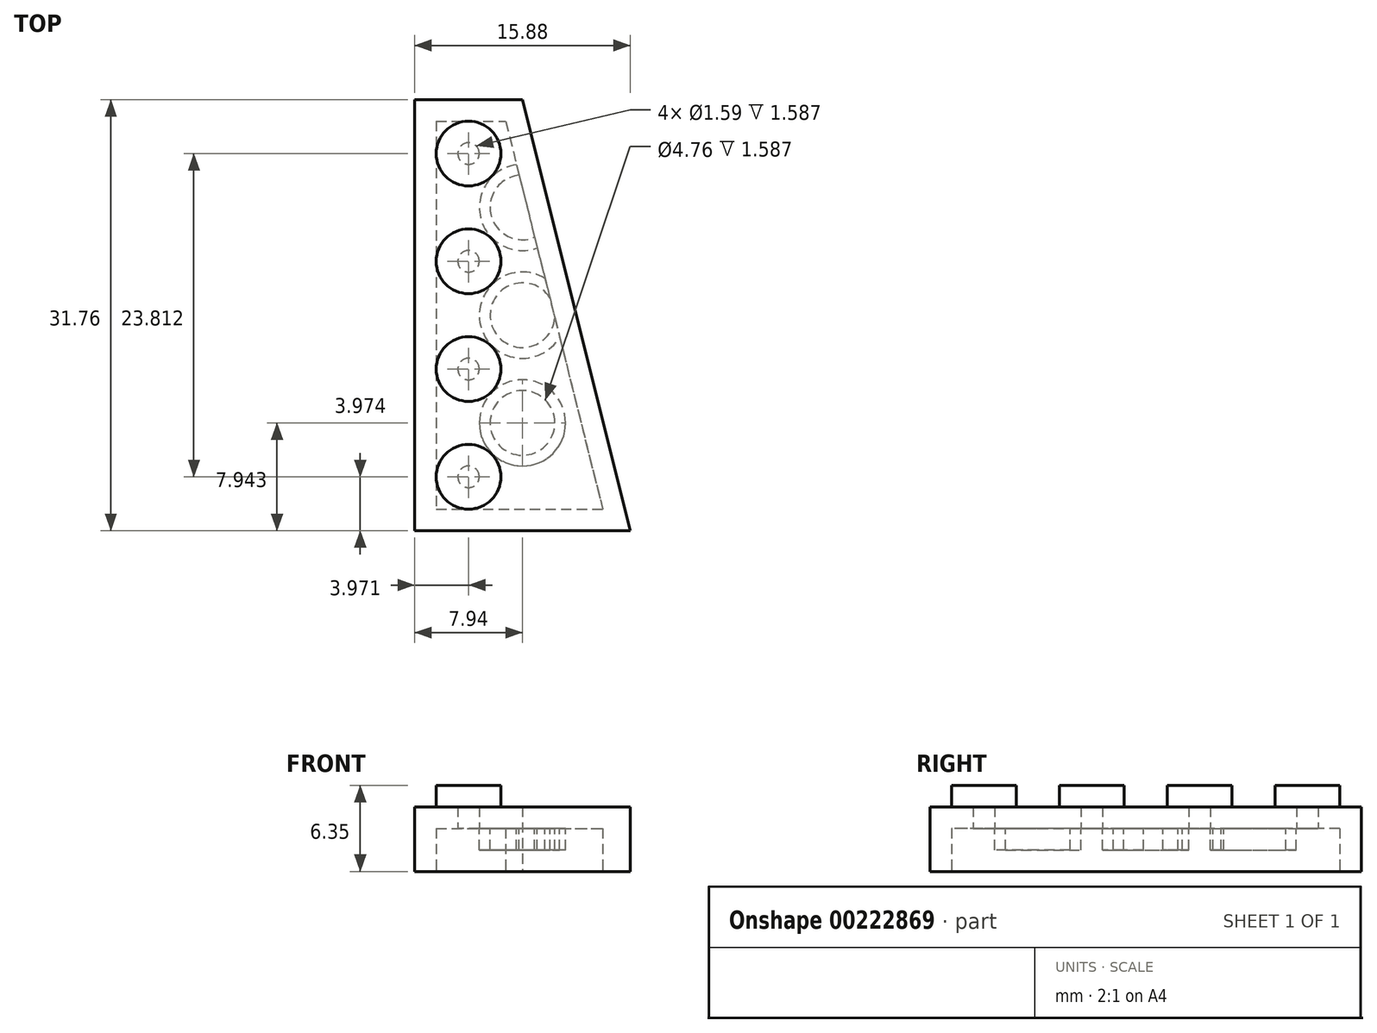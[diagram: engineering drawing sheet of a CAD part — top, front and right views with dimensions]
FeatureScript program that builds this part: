
annotation { "Feature Type Name" : "Feature", "Feature Type Description" : "" }
export const myFeature = defineFeature(function(context is Context, id is Id, definition is map)
    precondition{}
    {
        {
            var Q0;
            Q0=qCreatedBy(makeId("Top.planeOp"),FACE);
            var sketch = newSketch(context, id + "F0", { "sketchPlane" : qUnion([Q0])});
            skLineSegment(sketch, "E0.bottom", {"start": v(-7.94, 15.88) * mm, "end": v(7.94, 15.88) * mm});
            skLineSegment(sketch, "E0.top", {"start": v(-7.94, -15.88) * mm, "end": v(7.94, -15.88) * mm});
            skLineSegment(sketch, "E0.left", {"start": v(-7.94, 15.88) * mm, "end": v(-7.94, -15.88) * mm});
            skLineSegment(sketch, "E0.right", {"start": v(7.94, 15.88) * mm, "end": v(7.94, -15.88) * mm});
            skPoint(sketch, "E0.middle", {"position": v(0, 0) * mm});
            skCircle(sketch, "E1", {"center": v(-3.97, -11.9) * mm, "radius": 2.38 * mm});
            skCircle(sketch, "E2.0.1.0", {"center": v(-3.97, -3.97) * mm, "radius": 2.38 * mm});
            skLineSegment(sketch, "E2.direction1", {"start": v(-3.97, -11.9) * mm, "end": v(29.37, -11.9) * mm, "construction": true});
            skLineSegment(sketch, "E2.direction2", {"start": v(-3.97, -11.9) * mm, "end": v(-3.97, -3.97) * mm, "construction": true});
            skCircle(sketch, "E3.0.0.2", {"center": v(-3.97, 3.97) * mm, "radius": 2.38 * mm});
            skCircle(sketch, "E3.0.0.3", {"center": v(-3.97, 11.9) * mm, "radius": 2.38 * mm});
            skPoint(sketch, "E4", {"position": v(0, 15.88) * mm});
            skLineSegment(sketch, "E5", {"start": v(0, 15.87) * mm, "end": v(7.94, -15.87) * mm});
            skSolve(sketch);
        }
        {
            var Q0;
            Q0=makeQuery(id+"F0.imprint","IMPRINT",FACE,{"disambiguationData":[TD([[makeQuery(id+"F0.imprint","IMPRINT",EDGE,{"derivedFrom":sQuery(id+"F0.wireOp",EDGE,"E0.top")}),1.0]])]});
            extrude(context, id + "F1", {"entities" : qUnion([Q0]), "depth" : 3.17 * mm});
        }
        {
            var Q0;
            Q0=makeQuery(id+"F0.imprint","IMPRINT",FACE,{"disambiguationData":[TD([[makeQuery(id+"F0.imprint","IMPRINT",EDGE,{"derivedFrom":sQuery(id+"F0.wireOp",EDGE,"E3.0.0.3")}),1.0]])]});
            var Q1;
            Q1=makeQuery(id+"F0.imprint","IMPRINT",FACE,{"disambiguationData":[TD([[makeQuery(id+"F0.imprint","IMPRINT",EDGE,{"derivedFrom":sQuery(id+"F0.wireOp",EDGE,"E3.0.0.2")}),1.0]])]});
            var Q2;
            Q2=makeQuery(id+"F0.imprint","IMPRINT",FACE,{"disambiguationData":[TD([[makeQuery(id+"F0.imprint","IMPRINT",EDGE,{"derivedFrom":sQuery(id+"F0.wireOp",EDGE,"E2.0.1.0")}),1.0]])]});
            var Q3;
            Q3=makeQuery(id+"F0.imprint","IMPRINT",FACE,{"disambiguationData":[TD([[makeQuery(id+"F0.imprint","IMPRINT",EDGE,{"derivedFrom":sQuery(id+"F0.wireOp",EDGE,"E1")}),1.0]])]});
            extrude(context, id + "F2", {"entities" : qUnion([Q0, Q1, Q2, Q3]), "operationType" : NewBodyOperationType.ADD, "depth" : 4.76 * mm});
        }
        {
            var Q0;
            {var subQ0=sQuery(id+"F0.wireOp",EDGE,"E3.0.0.3");var subQ1=sQuery(id+"F0.wireOp",EDGE,"E3.0.0.2");var subQ2=sQuery(id+"F0.wireOp",EDGE,"E2.0.1.0");var subQ3=sQuery(id+"F0.wireOp",EDGE,"E1");Q0=makeQuery(id+"F2.boolean.opBoolean","MERGE",FACE,{"derivedFrom":[makeQuery(id+"F1.opExtrude","CAP_FACE",FACE,{"disambiguationData":[OSD([sQuery(id+"F0.wireOp",EDGE,"E0.bottom"),sQuery(id+"F0.wireOp",EDGE,"E0.top"),sQuery(id+"F0.wireOp",EDGE,"E0.left"),sQuery(id+"F0.wireOp",EDGE,"E0.right"),subQ3,subQ2,subQ1,subQ0])],"isStart":true}),makeQuery(id+"F2.opExtrude","CAP_FACE",FACE,{"disambiguationData":[OSD([subQ3])],"isStart":true}),makeQuery(id+"F2.opExtrude","CAP_FACE",FACE,{"disambiguationData":[OSD([subQ2])],"isStart":true}),makeQuery(id+"F2.opExtrude","CAP_FACE",FACE,{"disambiguationData":[OSD([subQ1])],"isStart":true}),makeQuery(id+"F2.opExtrude","CAP_FACE",FACE,{"disambiguationData":[OSD([subQ0])],"isStart":true})]});}
            shell(context, id + "F3", {"entities" : qUnion([Q0]), "thickness" : 1.59 * mm});
        }
        {
            var Q0;
            Q0=makeQuery(id+"F3.opShell","OFFSET_FACE",FACE,{"disambiguationData":[OSD([sQuery(id+"F0.wireOp",EDGE,"E0.bottom"),sQuery(id+"F0.wireOp",EDGE,"E0.top"),sQuery(id+"F0.wireOp",EDGE,"E0.left"),sQuery(id+"F0.wireOp",EDGE,"E1"),sQuery(id+"F0.wireOp",EDGE,"E2.0.1.0"),sQuery(id+"F0.wireOp",EDGE,"E3.0.0.2"),sQuery(id+"F0.wireOp",EDGE,"E3.0.0.3"),sQuery(id+"F0.wireOp",EDGE,"E5")])]});
            var sketch = newSketch(context, id + "F4", { "sketchPlane" : qUnion([Q0])});
            skCircle(sketch, "E6", {"center": v(0, -7.94) * mm, "radius": 3.18 * mm});
            skCircle(sketch, "E7", {"center": v(0, -7.94) * mm, "radius": 2.38 * mm});
            skCircle(sketch, "E8.0.1.0", {"center": v(0, 0) * mm, "radius": 3.18 * mm});
            skCircle(sketch, "E8.0.1.1", {"center": v(0, 0) * mm, "radius": 2.38 * mm});
            skCircle(sketch, "E8.0.2.0", {"center": v(0, 7.94) * mm, "radius": 3.18 * mm});
            skCircle(sketch, "E8.0.2.1", {"center": v(0, 7.94) * mm, "radius": 2.38 * mm});
            skLineSegment(sketch, "E8.direction1", {"start": v(0, -7.94) * mm, "end": v(25.4, -7.94) * mm, "construction": true});
            skLineSegment(sketch, "E8.direction2", {"start": v(0, -7.94) * mm, "end": v(0, 0) * mm, "construction": true});
            skSolve(sketch);
        }
        {
            var Q0;
            Q0=makeQuery(id+"F4.imprint","IMPRINT",FACE,{"disambiguationData":[TD([[makeQuery(id+"F4.imprint","IMPRINT",EDGE,{"derivedFrom":sQuery(id+"F4.wireOp",EDGE,"E8.0.2.0")}),1.0]])]});
            var Q1;
            {var subQ0=sQuery(id+"F4.wireOp",EDGE,"E8.0.1.0");var subQ1=sQuery(id+"F0.wireOp",EDGE,"Vv1mUmgO-7Zh7-OptV-hwL2-uFvwZgxB2kij");var subQ2=makeQuery(id+"F3.opShell","OFFSET_EDGE",EDGE,{"disambiguationData":[OSD([subQ1]),TDD([makeQuery(id+"F1.opExtrude","CAP_EDGE",EDGE,{"disambiguationData":[OSD([subQ1])],"isStart":false})])]});var subQ3=makeQuery(id+"F4.imprint","INTERSECT",VERTEX,{"disambiguationData":[OD(0.0)],"derivedFrom":[subQ2,subQ0]});Q1=makeQuery(id+"F4.imprint","IMPRINT",FACE,{"disambiguationData":[TD([[makeQuery(id+"F4.imprint","IMPRINT",EDGE,{"disambiguationData":[TD([[subQ3,1.0]])],"derivedFrom":subQ0}),1.0]])]});}
            var Q2;
            {var subQ0=sQuery(id+"F0.wireOp",EDGE,"E3.0.0.3");var subQ1=sQuery(id+"F0.wireOp",EDGE,"E3.0.0.2");var subQ2=sQuery(id+"F0.wireOp",EDGE,"E2.0.1.0");var subQ3=sQuery(id+"F0.wireOp",EDGE,"E1");Q2=makeQuery(id+"F2.boolean.opBoolean","MERGE",FACE,{"derivedFrom":[makeQuery(id+"F1.opExtrude","CAP_FACE",FACE,{"disambiguationData":[OSD([sQuery(id+"F0.wireOp",EDGE,"E0.bottom"),sQuery(id+"F0.wireOp",EDGE,"E0.top"),sQuery(id+"F0.wireOp",EDGE,"E0.left"),subQ3,subQ2,subQ1,subQ0,sQuery(id+"F0.wireOp",EDGE,"E5")])],"isStart":true}),makeQuery(id+"F2.opExtrude","CAP_FACE",FACE,{"disambiguationData":[OSD([subQ3])],"isStart":true}),makeQuery(id+"F2.opExtrude","CAP_FACE",FACE,{"disambiguationData":[OSD([subQ2])],"isStart":true}),makeQuery(id+"F2.opExtrude","CAP_FACE",FACE,{"disambiguationData":[OSD([subQ1])],"isStart":true}),makeQuery(id+"F2.opExtrude","CAP_FACE",FACE,{"disambiguationData":[OSD([subQ0])],"isStart":true})]});}
            var Q3;
            {var subQ0=sQuery(id+"F4.wireOp",EDGE,"E8.0.1.0");var subQ1=sQuery(id+"F0.wireOp",EDGE,"E5");var subQ2=makeQuery(id+"F3.opShell","OFFSET_EDGE",EDGE,{"disambiguationData":[OSD([subQ1]),TDD([makeQuery(id+"F1.opExtrude","CAP_EDGE",EDGE,{"disambiguationData":[OSD([subQ1])],"isStart":false})])]});var subQ3=makeQuery(id+"F4.imprint","INTERSECT",VERTEX,{"disambiguationData":[OD(0.0)],"derivedFrom":[subQ2,subQ0]});Q3=makeQuery(id+"F4.imprint","IMPRINT",FACE,{"disambiguationData":[TD([[makeQuery(id+"F4.imprint","IMPRINT",EDGE,{"disambiguationData":[TD([[subQ3,-1.0]])],"derivedFrom":subQ0}),1.0]])]});}
            var Q4;
            {var subQ0=sQuery(id+"F4.wireOp",EDGE,"E6");var subQ1=sQuery(id+"F0.wireOp",EDGE,"E5");var subQ2=makeQuery(id+"F3.opShell","OFFSET_EDGE",EDGE,{"disambiguationData":[OSD([subQ1]),TDD([makeQuery(id+"F1.opExtrude","CAP_EDGE",EDGE,{"disambiguationData":[OSD([subQ1])],"isStart":false})])]});var subQ3=makeQuery(id+"F4.imprint","INTERSECT",VERTEX,{"disambiguationData":[OD(0.0)],"derivedFrom":[subQ2,subQ0]});Q4=makeQuery(id+"F4.imprint","IMPRINT",FACE,{"disambiguationData":[TD([[makeQuery(id+"F4.imprint","IMPRINT",EDGE,{"disambiguationData":[TD([[subQ3,1.0]])],"derivedFrom":subQ0}),1.0]])]});}
            extrude(context, id + "F5", {"entities" : qUnion([Q0, Q1, Q2, Q3, Q4]), "operationType" : NewBodyOperationType.ADD, "depth" : 1.59 * mm});
        }
    });
